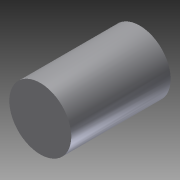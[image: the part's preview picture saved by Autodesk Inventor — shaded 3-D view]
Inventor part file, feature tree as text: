
AUTODESK INVENTOR PART (.ipt)
format: ipt  version: 2016 SP1 (Build 200210100, 210)  size: 83,968 bytes
history: native  units: in
note: dims shown in document units (in); Inventor stores cm internally (conversion verified against a paired STEP export)
features: plane x1, extrude x1, sketch x1, reference x1
ambient origin geometry x8: Origin, YZ Plane, XZ Plane, XY Plane, X Axis, Y Axis, Z Axis, Center Point
bodies: Solid1 (feature_tree)
feature tree (4):
  plane  "Work Plane1"
  extrude  "Extrusion1"  Depth=3.358in TaperAngle=0.0deg
  sketch  "Sketch1"  dims[d0=2.11in d1=3.358in d2=0.0in]
  reference  "Reference1"
